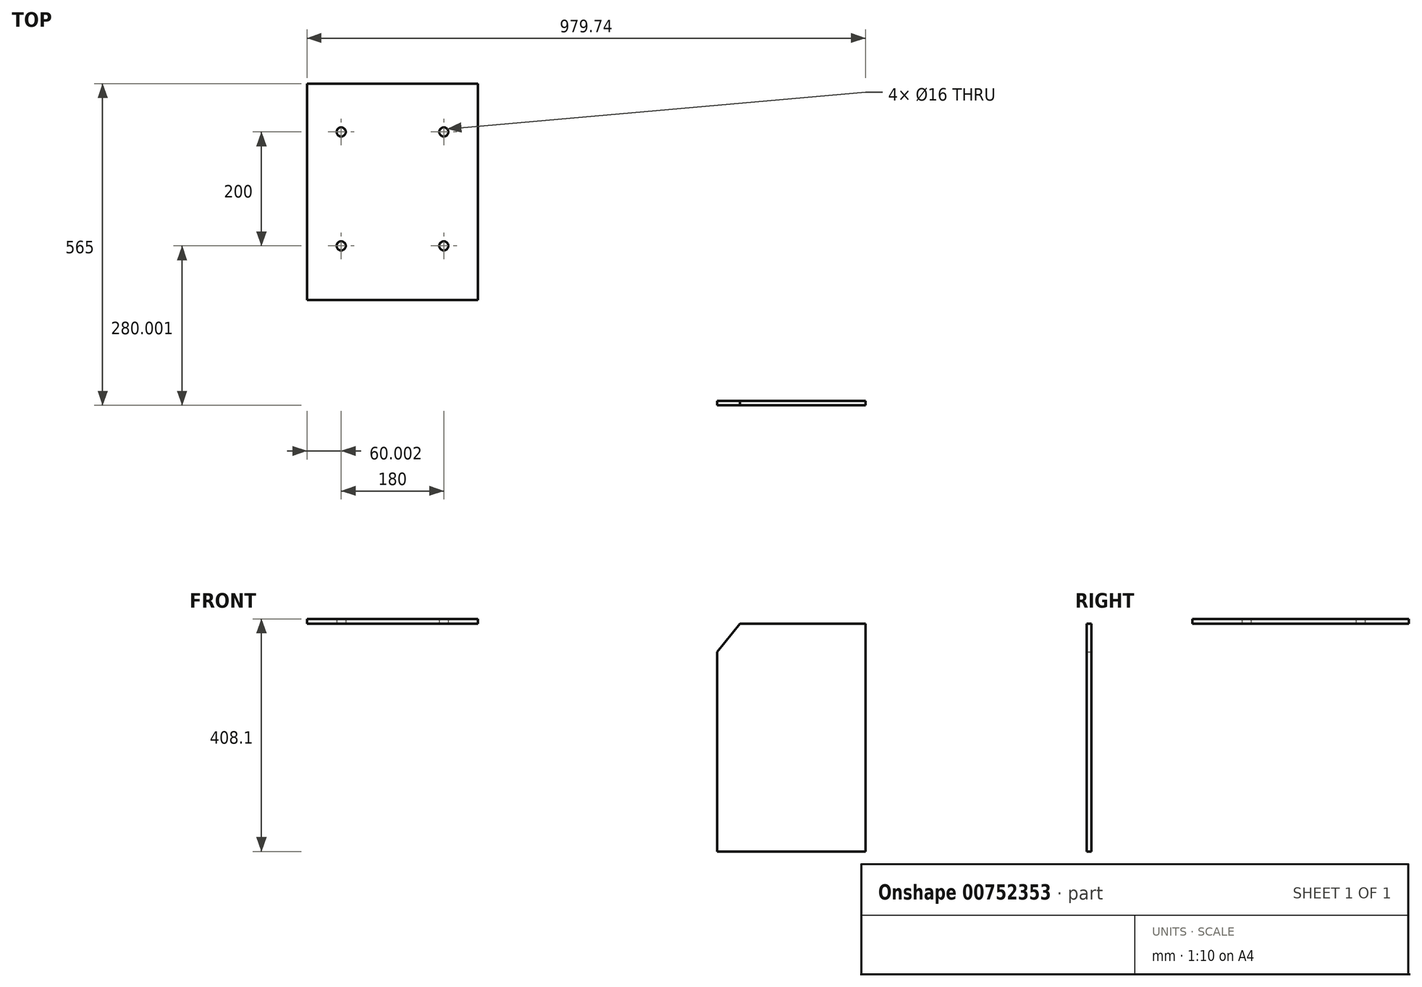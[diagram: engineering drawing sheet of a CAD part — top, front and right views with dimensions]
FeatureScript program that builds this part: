
annotation { "Feature Type Name" : "Feature", "Feature Type Description" : "" }
export const myFeature = defineFeature(function(context is Context, id is Id, definition is map)
    precondition{}
    {
        {
            var Q0;
            Q0=qCreatedBy(makeId("Front.planeOp"),FACE);
            var sketch = newSketch(context, id + "F0", { "sketchPlane" : qUnion([Q0])});
            skLineSegment(sketch, "E0", {"start": v(0, 0) * mm, "end": v(220, 0) * mm});
            skLineSegment(sketch, "E1", {"start": v(220, 0) * mm, "end": v(220, -400) * mm});
            skLineSegment(sketch, "E2", {"start": v(220, -400) * mm, "end": v(-40, -400) * mm});
            skLineSegment(sketch, "E3", {"start": v(-40, -400) * mm, "end": v(-40, -50) * mm});
            skLineSegment(sketch, "E4", {"start": v(-40, -50) * mm, "end": v(0, 0) * mm});
            skSolve(sketch);
        }
        {
            var Q0;
            Q0=makeQuery(id+"F0.imprint","IMPRINT",FACE,{"disambiguationData":[TD([[makeQuery(id+"F0.imprint","IMPRINT",EDGE,{"derivedFrom":sQuery(id+"F0.wireOp",EDGE,"E0")}),-1.0]])]});
            extrude(context, id + "F1", {"entities" : qUnion([Q0]), "depth" : 8.1 * mm, "offsetDistance" : 25 * mm});
        }
        {
            var Q0;
            Q0=qCreatedBy(makeId("Top.planeOp"),FACE);
            var sketch = newSketch(context, id + "F2", { "sketchPlane" : qUnion([Q0])});
            skLineSegment(sketch, "E5", {"start": v(-759.74, 556.9) * mm, "end": v(-459.74, 556.9) * mm});
            skLineSegment(sketch, "E6", {"start": v(-459.74, 556.9) * mm, "end": v(-459.74, 176.9) * mm});
            skLineSegment(sketch, "E7", {"start": v(-459.74, 176.9) * mm, "end": v(-759.74, 176.9) * mm});
            skLineSegment(sketch, "E8", {"start": v(-759.74, 176.9) * mm, "end": v(-759.74, 556.9) * mm});
            skPoint(sketch, "E9", {"position": v(-699.74, 471.9) * mm});
            skPoint(sketch, "E10", {"position": v(-519.74, 471.9) * mm});
            skPoint(sketch, "E11", {"position": v(-699.74, 271.9) * mm});
            skPoint(sketch, "E12", {"position": v(-519.74, 271.9) * mm});
            skSolve(sketch);
        }
        {
            var Q0;
            Q0=makeQuery(id+"F2.imprint","IMPRINT",FACE,{"disambiguationData":[TD([[makeQuery(id+"F2.imprint","IMPRINT",EDGE,{"derivedFrom":sQuery(id+"F2.wireOp",EDGE,"E5")}),-1.0]])]});
            extrude(context, id + "F3", {"entities" : qUnion([Q0]), "depth" : 8.1 * mm, "offsetDistance" : 25 * mm});
        }
        {
            var Q0;
            Q0=sQuery(id+"F2.wireOp",VERTEX,"E10");
            var Q1;
            Q1=sQuery(id+"F2.wireOp",VERTEX,"E9");
            var Q2;
            Q2=sQuery(id+"F2.wireOp",VERTEX,"E11");
            var Q3;
            Q3=sQuery(id+"F2.wireOp",VERTEX,"E12");
            var Q4;
            Q4=makeQuery(id+"F3.opExtrude","SWEPT_BODY",BODY,{"disambiguationData":[OSD([sQuery(id+"F2.wireOp",EDGE,"E5"),sQuery(id+"F2.wireOp",EDGE,"E6"),sQuery(id+"F2.wireOp",EDGE,"E7"),sQuery(id+"F2.wireOp",EDGE,"E8")])]});
            hole(context, id + "F4", {"style" : HoleStyle.SIMPLE, "endStyle" : HoleEndStyle.THROUGH, "oppositeDirection" : true, "standardTappedOrClearance" : lookupTablePath({ "standard" : "ISO", "size" : "16", "type" : "Drilled" }), "standardBlindInLast" : lookupTablePath({ "standard" : "ISO", "size" : "16", "type" : "Drilled" }), "holeDiameter" : 16 * mm, "majorDiameter" : 5 * mm, "isTappedThrough" : true, "tappedDepth" : 12 * mm, "tapClearance" : 3, "locations" : qUnion([Q0, Q1, Q2, Q3]), "scope" : qUnion([Q4])});
        }
    });
